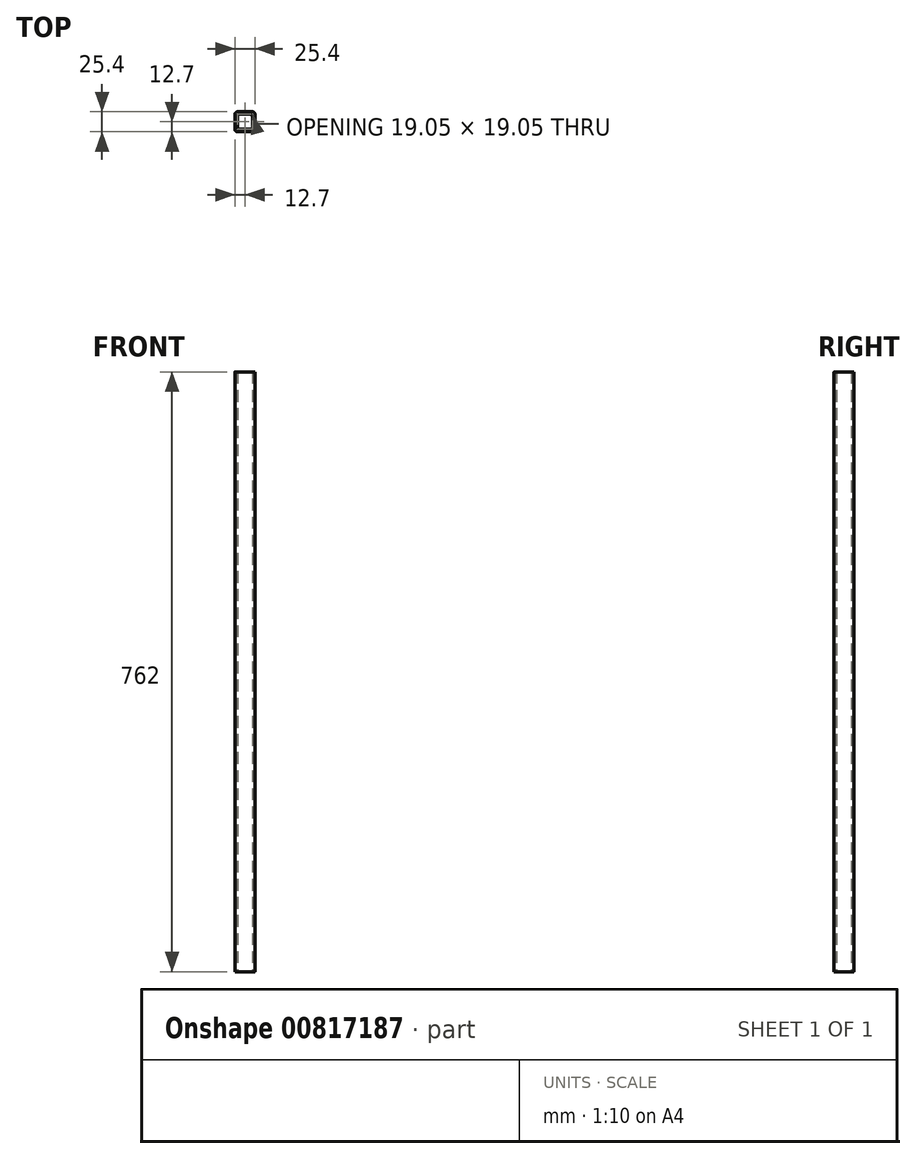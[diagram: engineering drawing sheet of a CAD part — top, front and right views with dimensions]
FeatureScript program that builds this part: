
annotation { "Feature Type Name" : "Feature", "Feature Type Description" : "" }
export const myFeature = defineFeature(function(context is Context, id is Id, definition is map)
    precondition{}
    {
        {
            var Q0;
            Q0=qCreatedBy(makeId("Top.planeOp"),FACE);
            var sketch = newSketch(context, id + "F0", { "sketchPlane" : qUnion([Q0])});
            skLineSegment(sketch, "E0.bottom", {"start": v(9.52, 12.7) * mm, "end": v(-9.53, 12.7) * mm});
            skLineSegment(sketch, "E0.top", {"start": v(9.53, -12.7) * mm, "end": v(-9.52, -12.7) * mm});
            skLineSegment(sketch, "E0.left", {"start": v(12.7, 9.53) * mm, "end": v(12.7, -9.53) * mm});
            skLineSegment(sketch, "E0.right", {"start": v(-12.7, 9.53) * mm, "end": v(-12.7, -9.53) * mm});
            skPoint(sketch, "E0.middle", {"position": v(0, 0) * mm});
            skLineSegment(sketch, "E1.0", {"start": v(-9.53, 6.35) * mm, "end": v(-9.52, -6.35) * mm});
            skLineSegment(sketch, "E1.1", {"start": v(6.35, 9.53) * mm, "end": v(-6.35, 9.53) * mm});
            skLineSegment(sketch, "E1.2", {"start": v(9.52, 6.35) * mm, "end": v(9.53, -6.35) * mm});
            skLineSegment(sketch, "E1.3", {"start": v(6.35, -9.53) * mm, "end": v(-6.35, -9.53) * mm});
            skPoint(sketch, "E2.visualSharp", {"position": v(-12.7, 12.7) * mm});
            skArc(sketch, "E2.filletArc", {"start": v(-9.53, 12.7) * mm, "mid": v(-11.77, 11.77) * mm, "end": v(-12.7, 9.53) * mm});
            skPoint(sketch, "E3.visualSharp", {"position": v(9.52, 9.53) * mm});
            skArc(sketch, "E3.filletArc", {"start": v(9.52, 6.35) * mm, "mid": v(8.6, 8.6) * mm, "end": v(6.35, 9.53) * mm});
            skPoint(sketch, "E4.visualSharp", {"position": v(12.7, 12.7) * mm});
            skArc(sketch, "E4.filletArc", {"start": v(12.7, 9.53) * mm, "mid": v(11.77, 11.77) * mm, "end": v(9.52, 12.7) * mm});
            skPoint(sketch, "E5.visualSharp", {"position": v(-12.7, -12.7) * mm});
            skArc(sketch, "E5.filletArc", {"start": v(-12.7, -9.53) * mm, "mid": v(-11.77, -11.77) * mm, "end": v(-9.52, -12.7) * mm});
            skPoint(sketch, "E6.visualSharp", {"position": v(12.7, -12.7) * mm});
            skArc(sketch, "E6.filletArc", {"start": v(9.53, -12.7) * mm, "mid": v(11.77, -11.77) * mm, "end": v(12.7, -9.53) * mm});
            skArc(sketch, "E7.filletArc", {"start": v(-6.35, 9.53) * mm, "mid": v(-8.6, 8.6) * mm, "end": v(-9.53, 6.35) * mm});
            skPoint(sketch, "E8.visualSharp", {"position": v(-9.52, -9.53) * mm});
            skArc(sketch, "E8.filletArc", {"start": v(-9.52, -6.35) * mm, "mid": v(-8.6, -8.6) * mm, "end": v(-6.35, -9.53) * mm});
            skPoint(sketch, "E9.visualSharp", {"position": v(9.53, -9.53) * mm});
            skArc(sketch, "E9.filletArc", {"start": v(6.35, -9.53) * mm, "mid": v(8.6, -8.6) * mm, "end": v(9.53, -6.35) * mm});
            skSolve(sketch);
        }
        {
            var Q0;
            Q0=makeQuery(id+"F0.imprint","IMPRINT",FACE,{"disambiguationData":[TD([[makeQuery(id+"F0.imprint","IMPRINT",EDGE,{"derivedFrom":sQuery(id+"F0.wireOp",EDGE,"E0.bottom")}),1.0]])]});
            extrude(context, id + "F1", {"entities" : qUnion([Q0]), "depth" : 381 * mm, "offsetDistance" : 25.4 * mm, "hasSecondDirection" : true, "secondDirectionOppositeDirection" : true, "secondDirectionDepth" : 381 * mm});
        }
        {
            var Q0;
            Q0=makeQuery(id+"F1.opExtrude","SWEPT_FACE",FACE,{"disambiguationData":[OSD([sQuery(id+"F0.wireOp",EDGE,"E0.bottom")])]});
            cPlane(context, id + "F2", {"entities" : qUnion([Q0]), "cplaneType" : CPlaneType.OFFSET, "offset" : 0 * mm, "width" : 152.4 * mm, "height" : 152.4 * mm});
        }
    });
